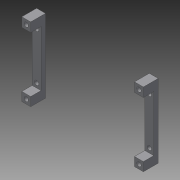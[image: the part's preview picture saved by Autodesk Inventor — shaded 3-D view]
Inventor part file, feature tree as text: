
AUTODESK INVENTOR PART (.ipt)
format: ipt  version: 2015 (Build 190159000, 159)  size: 128,000 bytes
history: native  units: in
note: dims shown in document units (in); Inventor stores cm internally (conversion verified against a paired STEP export)
features: sketch x2, extrude x2, plane x1
ambient origin geometry x8: Origin, YZ Plane, XZ Plane, XY Plane, X Axis, Y Axis, Z Axis, Center Point
bodies: Body1 (feature_tree)
feature tree (5):
  sketch  "Sketch1"  dims[d9=0.7381in d10=0.8563in]
  plane  "Work Plane1"
  extrude  "Extrusion3"  Depth=0.8563in
  extrude  "Extrusion4"  Depth=0.1181in TaperAngle=0.0deg
  sketch  "Sketch4"  dims[d11=0.1181in d12=0.1181in d13=0.0in d18=0.3937in d19=0.0in]
